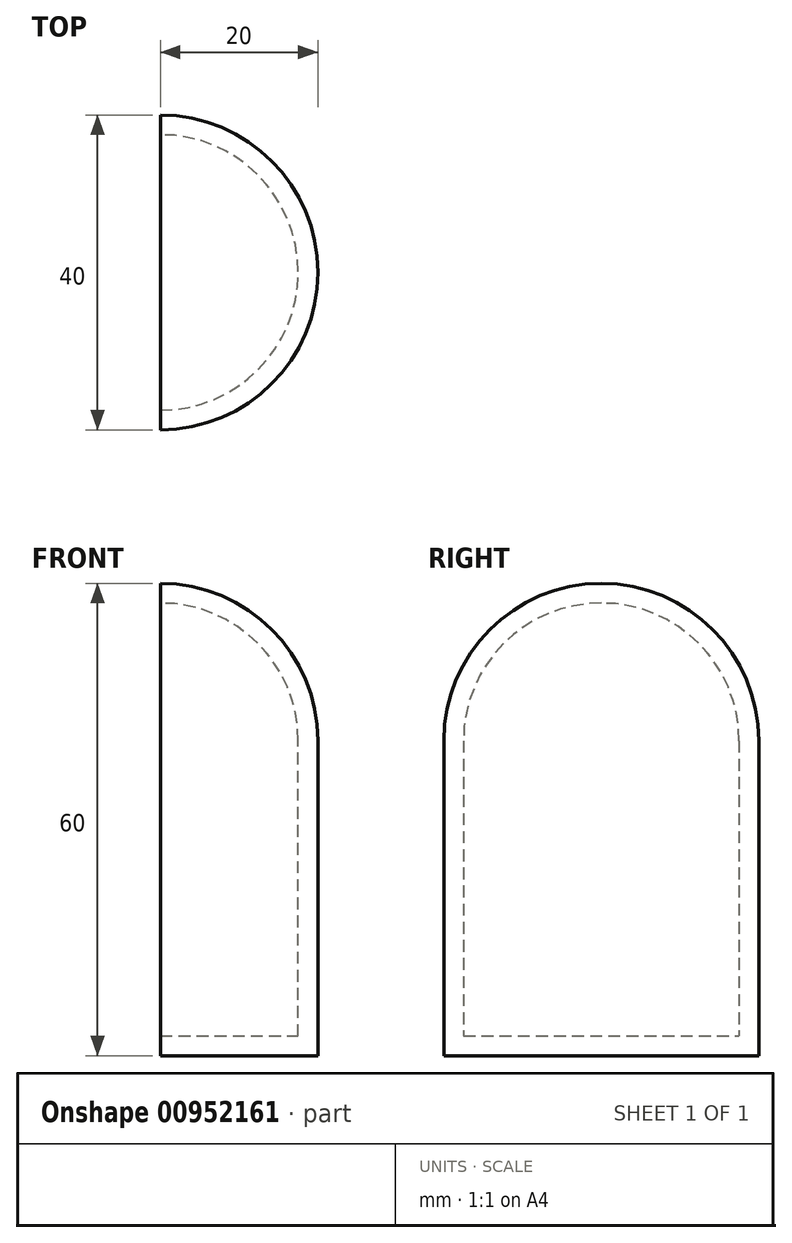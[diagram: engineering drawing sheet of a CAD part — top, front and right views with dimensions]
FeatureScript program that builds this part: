
annotation { "Feature Type Name" : "Feature", "Feature Type Description" : "" }
export const myFeature = defineFeature(function(context is Context, id is Id, definition is map)
    precondition{}
    {
        {
            var Q0;
            Q0=qCreatedBy(makeId("Front.planeOp"),FACE);
            var sketch = newSketch(context, id + "F0", { "sketchPlane" : qUnion([Q0])});
            skLineSegment(sketch, "E0", {"start": v(0, 0) * mm, "end": v(20, 0) * mm});
            skLineSegment(sketch, "E1", {"start": v(20, 0) * mm, "end": v(20, 40) * mm});
            skArc(sketch, "E2", {"start": v(20, 40) * mm, "mid": v(14.14, 54.14) * mm, "end": v(0, 60) * mm});
            skArc(sketch, "E3", {"start": v(17.5, 40) * mm, "mid": v(12.37, 52.37) * mm, "end": v(0, 57.5) * mm});
            skLineSegment(sketch, "E4", {"start": v(0, 60) * mm, "end": v(0, 57.5) * mm});
            skLineSegment(sketch, "E5", {"start": v(17.5, 40) * mm, "end": v(17.5, 2.5) * mm});
            skLineSegment(sketch, "E6", {"start": v(17.5, 2.5) * mm, "end": v(0, 2.5) * mm});
            skLineSegment(sketch, "E7", {"start": v(0, 2.5) * mm, "end": v(0, 0) * mm});
            skSolve(sketch);
        }
        {
            var Q0;
            Q0 = qSketchRegion(id + "F0", true);
            var Q1;
            Q1=sQuery(id+"F0.wireOp",EDGE,"E7");
            revolve(context, id + "F1", {"surfaceOperationType" : NewSurfaceOperationType.NEW, "entities" : qUnion([Q0]), "axis" : qUnion([Q1]), "revolveType" : RevolveType.SYMMETRIC, "angle" : 180 * degree});
        }
    });
